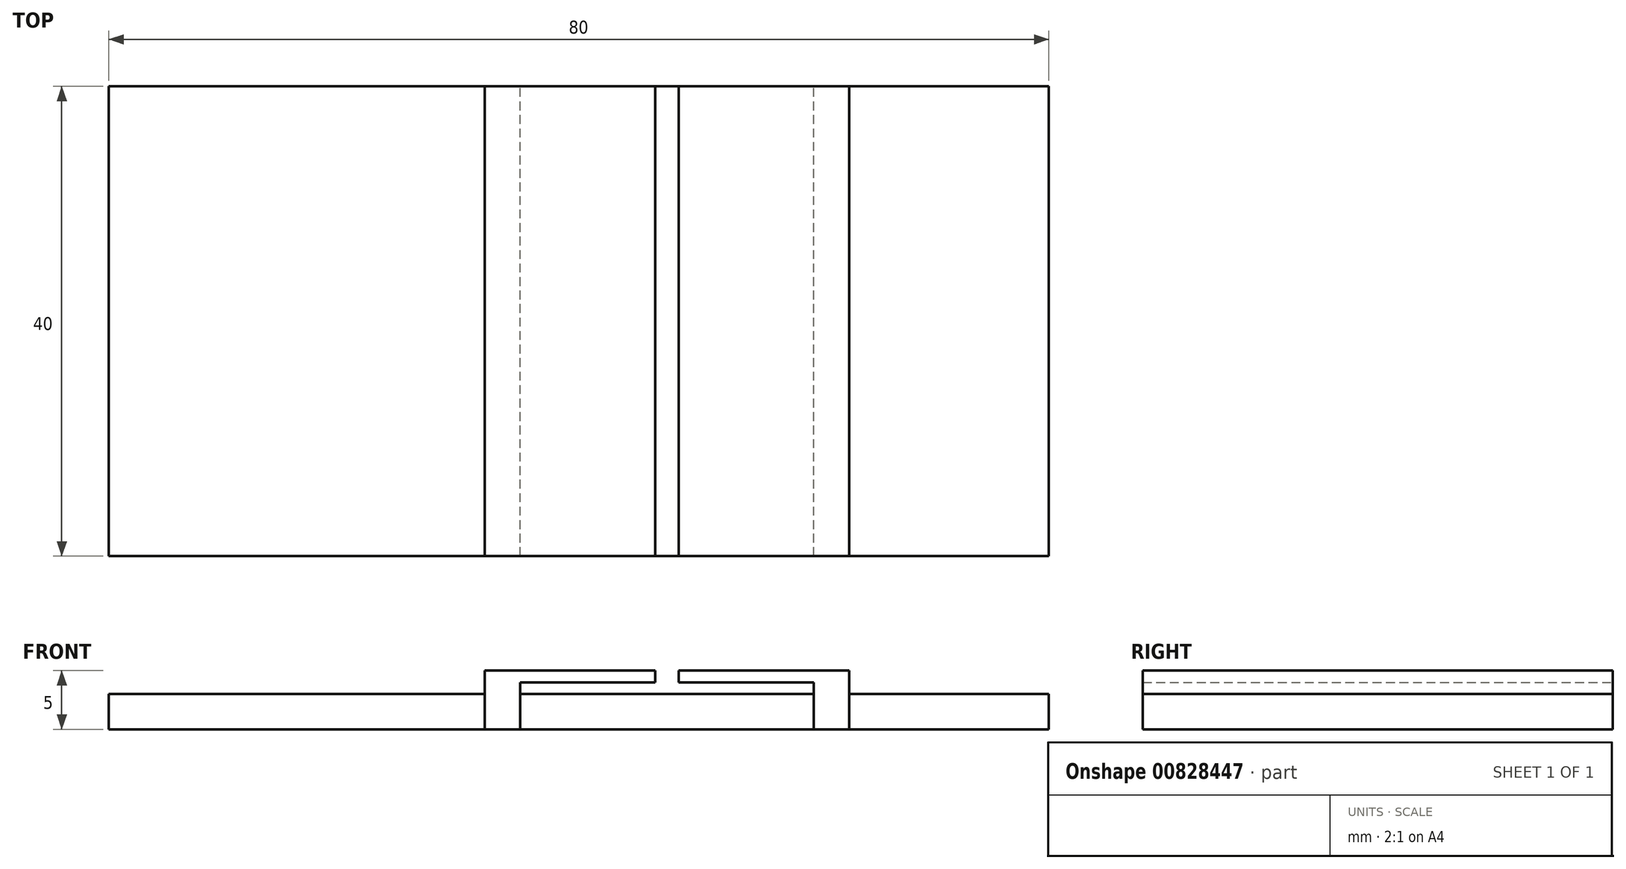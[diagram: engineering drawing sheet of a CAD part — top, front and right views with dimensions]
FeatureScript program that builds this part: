
annotation { "Feature Type Name" : "Feature", "Feature Type Description" : "" }
export const myFeature = defineFeature(function(context is Context, id is Id, definition is map)
    precondition{}
    {
        {
            var Q0;
            Q0=qCreatedBy(makeId("Top.planeOp"),FACE);
            var sketch = newSketch(context, id + "F0", { "sketchPlane" : qUnion([Q0])});
            skLineSegment(sketch, "E0.bottom", {"start": v(-36, 19.9) * mm, "end": v(44, 19.9) * mm});
            skLineSegment(sketch, "E0.top", {"start": v(-36, -20.1) * mm, "end": v(44, -20.1) * mm});
            skLineSegment(sketch, "E0.left", {"start": v(-36, 19.9) * mm, "end": v(-36, -20.1) * mm});
            skLineSegment(sketch, "E0.right", {"start": v(44, 19.9) * mm, "end": v(44, -20.1) * mm});
            skLineSegment(sketch, "E1", {"start": v(-4, -20.1) * mm, "end": v(-4, 19.9) * mm});
            skLineSegment(sketch, "E2", {"start": v(-4, 19.9) * mm, "end": v(-1, 19.9) * mm});
            skLineSegment(sketch, "E3", {"start": v(-1, 19.9) * mm, "end": v(-1, -20.1) * mm});
            skLineSegment(sketch, "E4", {"start": v(-1, -20.1) * mm, "end": v(-4, -20.1) * mm});
            skLineSegment(sketch, "E5", {"start": v(24, -20.1) * mm, "end": v(24, 19.9) * mm});
            skLineSegment(sketch, "E6", {"start": v(24, 19.9) * mm, "end": v(27, 19.9) * mm});
            skLineSegment(sketch, "E7", {"start": v(27, 19.9) * mm, "end": v(27, -20.1) * mm});
            skLineSegment(sketch, "E8", {"start": v(27, -20.1) * mm, "end": v(24, -20.1) * mm});
            skSolve(sketch);
        }
        {
            var Q0;
            {var subQ0=sQuery(id+"F0.wireOp",EDGE,"E0.left");Q0=makeQuery(id+"F0.imprint","IMPRINT",FACE,{"disambiguationData":[TD([[makeQuery(id+"F0.imprint","IMPRINT",EDGE,{"derivedFrom":subQ0}),1.0]])]});}
            var Q1;
            {var subQ0=sQuery(id+"F0.wireOp",EDGE,"E3");Q1=makeQuery(id+"F0.imprint","IMPRINT",FACE,{"disambiguationData":[TD([[makeQuery(id+"F0.imprint","IMPRINT",EDGE,{"derivedFrom":subQ0}),1.0]])]});}
            var Q2;
            {var subQ0=sQuery(id+"F0.wireOp",EDGE,"E0.right");Q2=makeQuery(id+"F0.imprint","IMPRINT",FACE,{"disambiguationData":[TD([[makeQuery(id+"F0.imprint","IMPRINT",EDGE,{"derivedFrom":subQ0}),-1.0]])]});}
            extrude(context, id + "F1", {"entities" : qUnion([Q0, Q1, Q2]), "depth" : 3 * mm, "offsetDistance" : 25.4 * mm});
        }
        {
            var Q0;
            Q0=makeQuery(id+"F0.imprint","IMPRINT",FACE,{"disambiguationData":[TD([[makeQuery(id+"F0.imprint","IMPRINT",EDGE,{"derivedFrom":sQuery(id+"F0.wireOp",EDGE,"E1")}),-1.0]])]});
            var Q1;
            Q1=makeQuery(id+"F0.imprint","IMPRINT",FACE,{"disambiguationData":[TD([[makeQuery(id+"F0.imprint","IMPRINT",EDGE,{"derivedFrom":sQuery(id+"F0.wireOp",EDGE,"E5")}),-1.0]])]});
            extrude(context, id + "F2", {"entities" : qUnion([Q0, Q1]), "depth" : 5 * mm, "offsetDistance" : 25.4 * mm});
        }
        {
            var Q0;
            Q0=makeQuery(id+"F2.opExtrude","SWEPT_FACE",FACE,{"disambiguationData":[OSD([sQuery(id+"F0.wireOp",EDGE,"E3")])]});
            var sketch = newSketch(context, id + "F3", { "sketchPlane" : qUnion([Q0])});
            skLineSegment(sketch, "E9", {"start": v(-20.1, 5) * mm, "end": v(-20.1, 4) * mm});
            skLineSegment(sketch, "E10", {"start": v(-20.1, 4) * mm, "end": v(19.9, 4) * mm});
            skLineSegment(sketch, "E11", {"start": v(19.9, 4) * mm, "end": v(19.9, 5) * mm});
            skLineSegment(sketch, "E12", {"start": v(19.9, 5) * mm, "end": v(-20.1, 5) * mm});
            skSolve(sketch);
        }
        {
            var Q0;
            Q0=makeQuery(id+"F3.imprint","IMPRINT",FACE,{"disambiguationData":[TD([[makeQuery(id+"F3.imprint","IMPRINT",EDGE,{"derivedFrom":sQuery(id+"F3.wireOp",EDGE,"E9")}),1.0]])]});
            extrude(context, id + "F4", {"entities" : qUnion([Q0]), "operationType" : NewBodyOperationType.ADD, "depth" : 11.5 * mm, "offsetDistance" : 25.4 * mm});
        }
        {
            var Q0;
            Q0=makeQuery(id+"F2.opExtrude","SWEPT_FACE",FACE,{"disambiguationData":[OSD([sQuery(id+"F0.wireOp",EDGE,"E5")])]});
            var sketch = newSketch(context, id + "F5", { "sketchPlane" : qUnion([Q0])});
            skLineSegment(sketch, "E13", {"start": v(-19.9, 5) * mm, "end": v(-19.9, 4) * mm});
            skLineSegment(sketch, "E14", {"start": v(-19.9, 4) * mm, "end": v(20.1, 4) * mm});
            skLineSegment(sketch, "E15", {"start": v(20.1, 4) * mm, "end": v(20.1, 5) * mm});
            skLineSegment(sketch, "E16", {"start": v(20.1, 5) * mm, "end": v(-19.9, 5) * mm});
            skSolve(sketch);
        }
        {
            var Q0;
            Q0=makeQuery(id+"F5.imprint","IMPRINT",FACE,{"disambiguationData":[TD([[makeQuery(id+"F5.imprint","IMPRINT",EDGE,{"derivedFrom":sQuery(id+"F5.wireOp",EDGE,"E13")}),1.0]])]});
            extrude(context, id + "F6", {"entities" : qUnion([Q0]), "operationType" : NewBodyOperationType.ADD, "depth" : 11.5 * mm, "offsetDistance" : 25.4 * mm});
        }
    });
